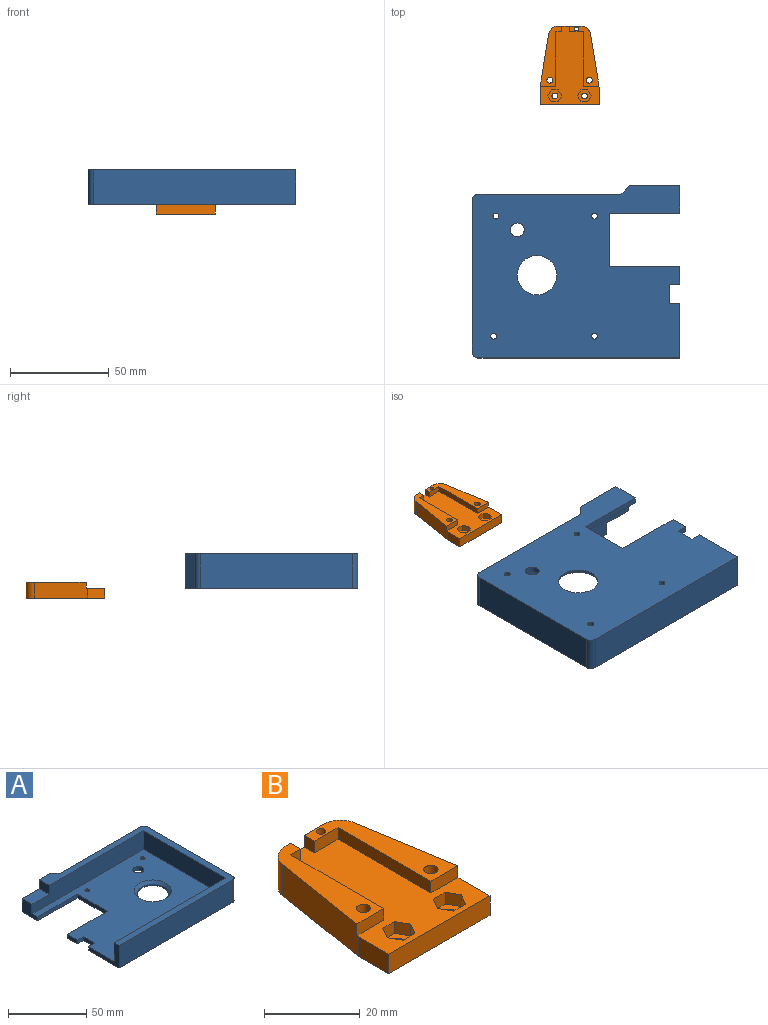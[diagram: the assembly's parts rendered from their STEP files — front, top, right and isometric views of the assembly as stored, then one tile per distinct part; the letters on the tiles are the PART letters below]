
ASSEMBLY  parts=2 mates=1
PART A: 31 faces, bbox 105.5x87.5x17.5 mm
  f0: plane 77x17.5mm, normal (1,0,0), area 1347.5mm2, adj f1,f15,f25,f26
  f1: cylinder r=3mm len=17.5mm, axis (0,0,1), area 82.5mm2, adj f0,f2,f25,f26
  f2: plane 72.5x17.5mm, normal (0,1,0), area 1268.8mm2, adj f1,f3,f25,f26
  f3: plane 17.5x4.5mm, normal (0.71,0.71,0), area 111.4mm2, adj f2,f25,f26,f27
  f4: cylinder r=10mm len=20mm, axis (0,0,-1), area 62.8mm2, adj f10,f25
  f5: cylinder r=3.5mm len=7mm, axis (0,0,-1), area 66mm2, adj f23,f25
  f6: cylinder r=1.5mm len=3mm, axis (0,0,-1), area 28.3mm2, adj f23,f25
  f7: cylinder r=1.5mm len=3mm, axis (0,0,-1), area 28.3mm2, adj f23,f25
  f8: cylinder r=1.5mm len=3mm, axis (0,0,-1), area 28.3mm2, adj f23,f25
  f9: cylinder r=1.5mm len=3mm, axis (0,0,-1), area 28.3mm2, adj f23,f25
  f10: cone r=10mm half-angle=45deg, axis (0,0,1), area 195.5mm2, adj f4,f23
  f11: plane 10x3mm, normal (-1,0,0), area 30mm2, adj f16,f17,f23,f25
  f12: plane 27x3mm, normal (-1,0,0), area 81mm2, adj f18,f19,f23,f25
  f13: plane 9x7mm, normal (-1,0,0), area 63mm2, adj f20,f21,f26,f27
  f14: plane 74x14.5mm, normal (-1,0,0), area 1073mm2, adj f20,f22,f23,f26
  f15: cylinder r=3mm len=17.5mm, axis (0,0,1), area 82.5mm2, adj f0,f24,f25,f26
  f16: plane 5.4x3mm, normal (0,1,0), area 16.2mm2, adj f11,f23,f25,f28
  f17: plane 5.4x3mm, normal (0,-1,0), area 16.2mm2, adj f11,f23,f25,f30
  f18: plane 36x3mm, normal (0,1,0), area 108mm2, adj f12,f23,f25,f30
  f19: plane 36x3mm, normal (0,-1,0), area 108mm2, adj f12,f23,f25,f29
  f20: plane 101x14.5mm, normal (0,-1,0), area 1356mm2, adj f13,f14,f21,f23,f26,f29
  f21: plane 15.5x9mm, normal (0,0,1), area 139.5mm2, adj f13,f20,f27,f29
  f22: plane 101x14.5mm, normal (0,1,0), area 1464.5mm2, adj f14,f23,f26,f28
  f23: plane 101x74mm, normal (0,0,1), area 5928.9mm2, adj f5,f6,f7,f8,f9,f10,f11,f12
  f24: plane 102.5x17.5mm, normal (0,-1,0), area 1793.7mm2, adj f15,f25,f26,f28
  f25: plane 105.5x87.5mm, normal (0,0,-1), area 7470.6mm2, adj f0,f1,f2,f3,f4,f5,f6,f7
  f26: plane 105.5x87.5mm, normal (0,0,1), area 1264mm2, adj f0,f1,f2,f3,f13,f14,f15,f20
  f27: plane 25.5x17.5mm, normal (0,1,0), area 337.8mm2, adj f3,f13,f21,f25,f26,f29
  f28: plane 27.5x17.5mm, normal (-1,0,0), area 147.8mm2, adj f16,f22,f23,f24,f25,f26
  f29: plane 14x10.5mm, normal (-1,0,0), area 109.5mm2, adj f19,f20,f21,f23,f25,f27
  f30: plane 9x3mm, normal (-1,0,0), area 27mm2, adj f17,f18,f23,f25
PART B: 57 faces, bbox 30x40x8 mm
  f0: plane 11.46x8mm, normal (0,1,0), area 65.4mm2, adj f10,f11,f33,f34,f35,f36,f51,f52
  f1: cylinder r=1mm len=5mm, axis (0,0,1), area 31.4mm2, adj f52,f56
  f2: plane 26.8x8mm, normal (0.99,0.16,0), area 215.6mm2, adj f10,f11,f15,f18,f33,f52
  f3: plane 26.8x8mm, normal (-0.99,0.16,0), area 215.7mm2, adj f10,f11,f14,f17,f34,f51
  f4: cylinder r=1.5mm len=5mm, axis (0,0,1), area 47.1mm2, adj f50,f51
  f5: cylinder r=1.5mm len=5mm, axis (0,0,1), area 47.1mm2, adj f43,f52
  f6: plane 7x3mm, normal (0,-1,0), area 21mm2, adj f7,f11,f36,f52
  f7: plane 27.5x3mm, normal (-1,0,0), area 82.5mm2, adj f6,f11,f18,f52
  f8: plane 27.5x3mm, normal (1,0,0), area 82.5mm2, adj f9,f11,f17,f51
  f9: plane 3x3mm, normal (0,-1,0), area 9mm2, adj f8,f11,f35,f51
  f10: plane 40x30mm, normal (0,0,-1), area 942.1mm2, adj f0,f2,f3,f12,f13,f14,f15,f16
  f11: plane 40x30mm, normal (0,0,1), area 618.3mm2, adj f0,f2,f3,f6,f7,f8,f9,f14
  f12: cylinder r=1.5mm len=3mm, axis (0,0,1), area 18.8mm2, adj f10,f32
  f13: cylinder r=1.5mm len=3mm, axis (0,0,1), area 18.8mm2, adj f10,f25
  f14: plane 9x5mm, normal (-1,0,0), area 45mm2, adj f3,f10,f11,f16
  f15: plane 9x5mm, normal (1,0,0), area 45mm2, adj f2,f10,f11,f16
  f16: plane 30x5mm, normal (0,-1,0), area 150mm2, adj f10,f11,f14,f15
  f17: plane 7.92x3mm, normal (0,-1,0), area 23.8mm2, adj f3,f8,f11,f51
  f18: plane 7.92x3mm, normal (0,-1,0), area 23.8mm2, adj f2,f7,f11,f52
  f19: plane 3.03x3mm, normal (-0.87,0.5,0), area 10.5mm2, adj f11,f20,f24,f25
  f20: plane 3.03x3mm, normal (-0.87,-0.5,0), area 10.5mm2, adj f11,f19,f21,f25
  f21: plane 3.5x3mm, normal (0,-1,0), area 10.5mm2, adj f11,f20,f22,f25
  f22: plane 3.03x3mm, normal (0.87,-0.5,0), area 10.5mm2, adj f11,f21,f23,f25
  f23: plane 3.03x3mm, normal (0.87,0.5,0), area 10.5mm2, adj f11,f22,f24,f25
  f24: plane 3.5x3mm, normal (0,1,0), area 10.5mm2, adj f11,f19,f23,f25
  f25: plane 7x6.06mm, normal (0,0,1), area 24.8mm2, adj f13,f19,f20,f21,f22,f23,f24
  f26: plane 3.03x3mm, normal (0.87,-0.5,0), area 10.5mm2, adj f11,f27,f31,f32
  f27: plane 3.03x3mm, normal (0.87,0.5,0), area 10.5mm2, adj f11,f26,f28,f32
  f28: plane 3.5x3mm, normal (0,1,0), area 10.5mm2, adj f11,f27,f29,f32
  f29: plane 3.03x3mm, normal (-0.87,0.5,0), area 10.5mm2, adj f11,f28,f30,f32
  f30: plane 3.03x3mm, normal (-0.87,-0.5,0), area 10.5mm2, adj f11,f29,f31,f32
  f31: plane 3.5x3mm, normal (0,-1,0), area 10.5mm2, adj f11,f26,f30,f32
  f32: plane 7x6.06mm, normal (0,0,1), area 24.8mm2, adj f12,f26,f27,f28,f29,f30,f31
  f33: cylinder r=5mm len=8mm, axis (0,0,-1), area 55.7mm2, adj f0,f2,f10,f52,f53,f56
  f34: cylinder r=5mm len=8mm, axis (0,0,1), area 56.4mm2, adj f0,f3,f10,f51
  f35: plane 3x3mm, normal (1,0,0), area 9mm2, adj f0,f9,f11,f51
  f36: plane 3x3mm, normal (-1,0,0), area 9mm2, adj f0,f6,f11,f52
  f37: plane 3.03x3mm, normal (0.87,0.5,0), area 10.5mm2, adj f10,f38,f42,f43
  f38: plane 3.03x3mm, normal (0.87,-0.5,0), area 10.5mm2, adj f10,f37,f39,f43
  f39: plane 3.5x3mm, normal (0,-1,0), area 10.5mm2, adj f10,f38,f40,f43
  f40: plane 3.03x3mm, normal (-0.87,-0.5,0), area 10.5mm2, adj f10,f39,f41,f43
  f41: plane 3.03x3mm, normal (-0.87,0.5,0), area 10.5mm2, adj f10,f40,f42,f43
  f42: plane 3.5x3mm, normal (0,1,0), area 10.5mm2, adj f10,f37,f41,f43
  f43: plane 7x6.06mm, normal (0,0,-1), area 24.8mm2, adj f5,f37,f38,f39,f40,f41,f42
  f44: plane 3.03x3mm, normal (-0.87,-0.5,0), area 10.5mm2, adj f10,f45,f49,f50
  f45: plane 3.03x3mm, normal (-0.87,0.5,0), area 10.5mm2, adj f10,f44,f46,f50
  f46: plane 3.5x3mm, normal (0,1,0), area 10.5mm2, adj f10,f45,f47,f50
  f47: plane 3.03x3mm, normal (0.87,0.5,0), area 10.5mm2, adj f10,f46,f48,f50
  f48: plane 3.03x3mm, normal (0.87,-0.5,0), area 10.5mm2, adj f10,f47,f49,f50
  f49: plane 3.5x3mm, normal (0,-1,0), area 10.5mm2, adj f10,f44,f48,f50
  f50: plane 7x6.06mm, normal (0,0,-1), area 24.8mm2, adj f4,f44,f45,f46,f47,f48,f49
  f51: plane 30.5x10.92mm, normal (0,0,1), area 164.3mm2, adj f0,f3,f4,f8,f9,f17,f34,f35
  f52: plane 30.5x14.92mm, normal (0,0,1), area 173.7mm2, adj f0,f1,f2,f5,f6,f7,f18,f33
  f53: plane 3x1.49mm, normal (-1,0,0), area 4.5mm2, adj f10,f33,f54,f56
  f54: cylinder r=2.5mm len=5mm, axis (0,0,-1), area 23.6mm2, adj f10,f53,f55,f56
  f55: plane 3x1.5mm, normal (1,0,0), area 4.5mm2, adj f0,f10,f54,f56
  f56: plane 5x4mm, normal (0,0,-1), area 14.2mm2, adj f0,f1,f33,f53,f54,f55
PLACE A rot(axis=(0,1,0),180deg) t=(2.27,-0.54,24.23)mm
PLACE B t=(2.27,-0.54,-12.27)mm
MATE fastened A.f26 <-> B.f11  axis (0,0,-1) through (-98.73,-37.54,6.73)mm
